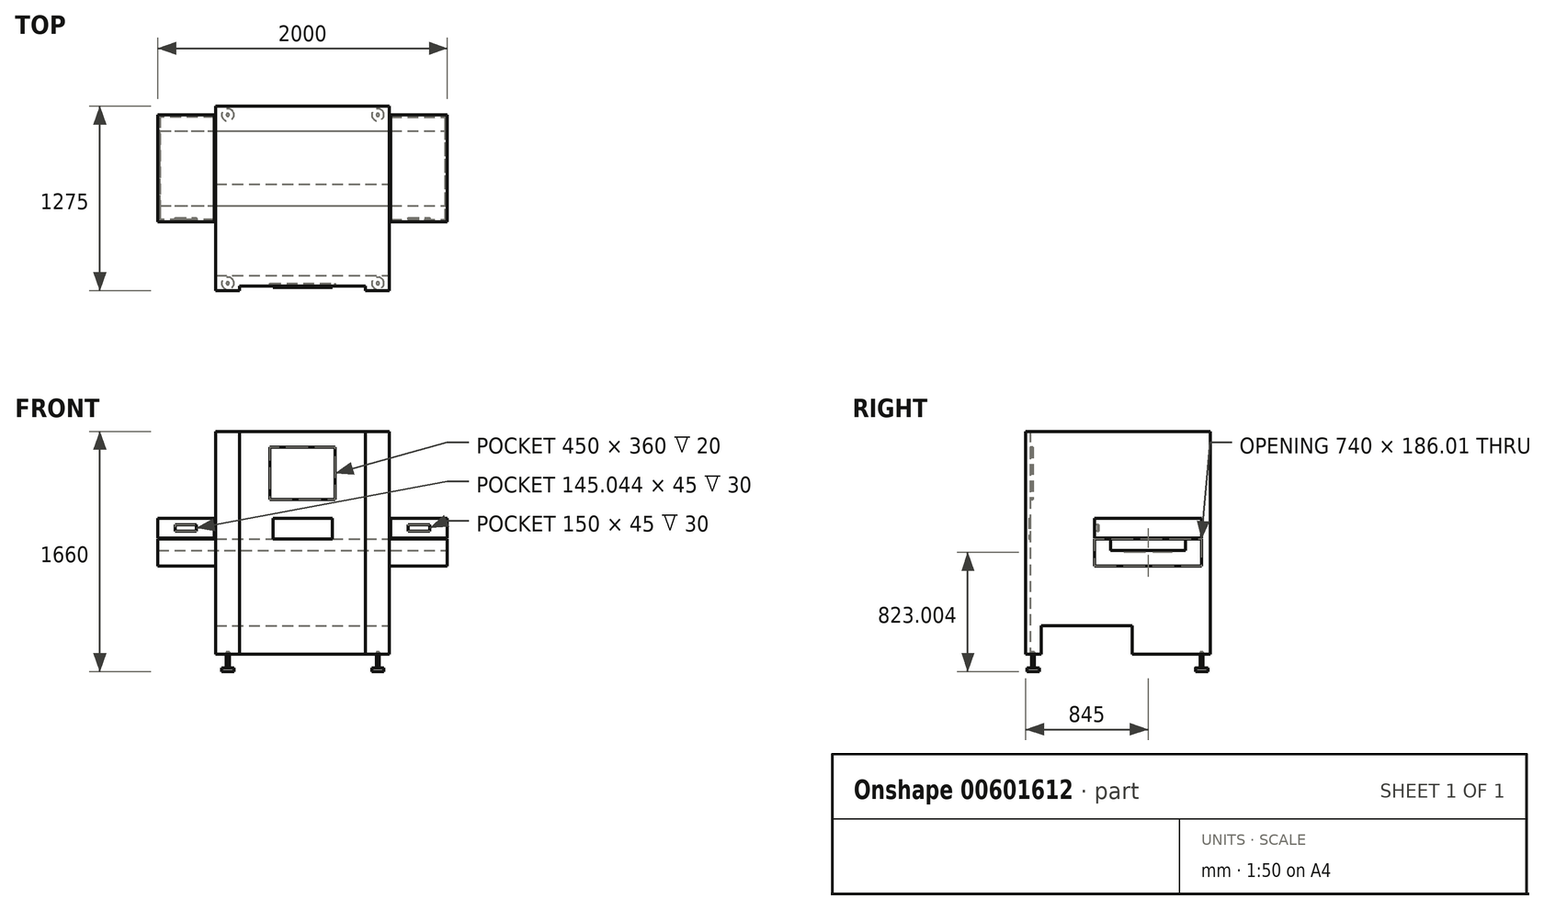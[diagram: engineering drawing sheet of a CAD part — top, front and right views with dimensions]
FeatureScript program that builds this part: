
annotation { "Feature Type Name" : "Feature", "Feature Type Description" : "" }
export const myFeature = defineFeature(function(context is Context, id is Id, definition is map)
    precondition{}
    {
        {
            var Q0;
            Q0=qCreatedBy(makeId("Top.planeOp"),FACE);
            var sketch = newSketch(context, id + "F0", { "sketchPlane" : qUnion([Q0])});
            skLineSegment(sketch, "E0.bottom", {"start": v(600, -637.5) * mm, "end": v(-600, -637.5) * mm});
            skLineSegment(sketch, "E0.top", {"start": v(600, 637.5) * mm, "end": v(-600, 637.5) * mm});
            skLineSegment(sketch, "E0.left", {"start": v(600, -637.5) * mm, "end": v(600, 637.5) * mm});
            skLineSegment(sketch, "E0.right", {"start": v(-600, -637.5) * mm, "end": v(-600, 637.5) * mm});
            skPoint(sketch, "E0.middle", {"position": v(0, 0) * mm});
            skSolve(sketch);
        }
        {
            var Q0;
            Q0=makeQuery(id+"F0.imprint","IMPRINT",FACE,{"disambiguationData":[TD([[makeQuery(id+"F0.imprint","IMPRINT",EDGE,{"derivedFrom":sQuery(id+"F0.wireOp",EDGE,"E0.bottom")}),-1.0]])]});
            extrude(context, id + "F1", {"entities" : qUnion([Q0]), "depth" : 1540 * mm, "offsetDistance" : 25 * mm});
        }
        {
            var Q0;
            Q0=makeQuery(id+"F1.opExtrude","CAP_FACE",FACE,{"disambiguationData":[OSD([sQuery(id+"F0.wireOp",EDGE,"E0.bottom"),sQuery(id+"F0.wireOp",EDGE,"E0.top"),sQuery(id+"F0.wireOp",EDGE,"E0.left"),sQuery(id+"F0.wireOp",EDGE,"E0.right")])],"isStart":true});
            var sketch = newSketch(context, id + "F2", { "sketchPlane" : qUnion([Q0])});
            skLineSegment(sketch, "E1.bottom", {"start": v(-600, 532.5) * mm, "end": v(600, 532.5) * mm});
            skLineSegment(sketch, "E1.top", {"start": v(-600, -97.5) * mm, "end": v(600, -97.5) * mm});
            skLineSegment(sketch, "E1.left", {"start": v(-600, 532.5) * mm, "end": v(-600, -97.5) * mm});
            skLineSegment(sketch, "E1.right", {"start": v(600, 532.5) * mm, "end": v(600, -97.5) * mm});
            skSolve(sketch);
        }
        {
            var Q0;
            Q0=makeQuery(id+"F2.imprint","IMPRINT",FACE,{"disambiguationData":[TD([[makeQuery(id+"F2.imprint","IMPRINT",EDGE,{"derivedFrom":sQuery(id+"F2.wireOp",EDGE,"E1.bottom")}),-1.0]])]});
            extrude(context, id + "F3", {"entities" : qUnion([Q0]), "operationType" : NewBodyOperationType.REMOVE, "oppositeDirection" : true, "depth" : 195 * mm, "offsetDistance" : 25 * mm});
        }
        {
            var Q0;
            Q0=makeQuery(id+"F1.opExtrude","SWEPT_FACE",FACE,{"disambiguationData":[OSD([sQuery(id+"F0.wireOp",EDGE,"E0.bottom")])]});
            var sketch = newSketch(context, id + "F4", { "sketchPlane" : qUnion([Q0])});
            skLineSegment(sketch, "E2.bottom", {"start": v(-435, 1540) * mm, "end": v(435, 1540) * mm});
            skLineSegment(sketch, "E2.top", {"start": v(-435, 0) * mm, "end": v(435, 0) * mm});
            skLineSegment(sketch, "E2.left", {"start": v(-435, 1540) * mm, "end": v(-435, 0) * mm});
            skLineSegment(sketch, "E2.right", {"start": v(435, 1540) * mm, "end": v(435, 0) * mm});
            skSolve(sketch);
        }
        {
            var Q0;
            Q0=makeQuery(id+"F4.imprint","IMPRINT",FACE,{"disambiguationData":[TD([[makeQuery(id+"F4.imprint","IMPRINT",EDGE,{"derivedFrom":sQuery(id+"F4.wireOp",EDGE,"E2.bottom")}),1.0]])]});
            extrude(context, id + "F5", {"entities" : qUnion([Q0]), "operationType" : NewBodyOperationType.REMOVE, "oppositeDirection" : true, "depth" : 30 * mm, "offsetDistance" : 25 * mm});
        }
        {
            var Q0;
            Q0=makeQuery(id+"F1.opExtrude","SWEPT_FACE",FACE,{"disambiguationData":[OSD([sQuery(id+"F0.wireOp",EDGE,"E0.left")])]});
            var sketch = newSketch(context, id + "F6", { "sketchPlane" : qUnion([Q0])});
            skLineSegment(sketch, "E3.bottom", {"start": v(-162.5, 940) * mm, "end": v(577.5, 940) * mm});
            skLineSegment(sketch, "E3.top", {"start": v(-162.5, 610) * mm, "end": v(577.5, 610) * mm});
            skLineSegment(sketch, "E3.left", {"start": v(-162.5, 940) * mm, "end": v(-162.5, 610) * mm});
            skLineSegment(sketch, "E3.right", {"start": v(577.5, 940) * mm, "end": v(577.5, 610) * mm});
            skSolve(sketch);
        }
        {
            var Q0;
            Q0=makeQuery(id+"F6.imprint","IMPRINT",FACE,{"disambiguationData":[TD([[makeQuery(id+"F6.imprint","IMPRINT",EDGE,{"derivedFrom":sQuery(id+"F6.wireOp",EDGE,"E3.bottom")}),-1.0]])]});
            extrude(context, id + "F7", {"entities" : qUnion([Q0]), "operationType" : NewBodyOperationType.ADD, "depth" : 400 * mm, "offsetDistance" : 25 * mm});
        }
        {
            var Q0;
            Q0=makeQuery(id+"F7.opExtrude","CAP_FACE",FACE,{"disambiguationData":[OSD([sQuery(id+"F6.wireOp",EDGE,"E3.bottom"),sQuery(id+"F6.wireOp",EDGE,"E3.top"),sQuery(id+"F6.wireOp",EDGE,"E3.left"),sQuery(id+"F6.wireOp",EDGE,"E3.right")])],"isStart":false});
            extrude(context, id + "F8", {"entities" : qUnion([Q0]), "operationType" : NewBodyOperationType.ADD, "oppositeDirection" : true, "depth" : 2000 * mm, "offsetDistance" : 25 * mm});
        }
        {
            var Q0;
            Q0=makeQuery(id+"F7.opExtrude","CAP_FACE",FACE,{"disambiguationData":[OSD([sQuery(id+"F6.wireOp",EDGE,"E3.bottom"),sQuery(id+"F6.wireOp",EDGE,"E3.top"),sQuery(id+"F6.wireOp",EDGE,"E3.left"),sQuery(id+"F6.wireOp",EDGE,"E3.right")])],"isStart":false});
            var sketch = newSketch(context, id + "F9", { "sketchPlane" : qUnion([Q0])});
            skLineSegment(sketch, "E4.bottom", {"start": v(-52.5, 796) * mm, "end": v(467.5, 796) * mm});
            skLineSegment(sketch, "E4.top", {"start": v(-52.5, 716) * mm, "end": v(467.5, 716) * mm});
            skLineSegment(sketch, "E4.left", {"start": v(-52.5, 796) * mm, "end": v(-52.5, 716) * mm});
            skLineSegment(sketch, "E4.right", {"start": v(467.5, 796) * mm, "end": v(467.5, 716) * mm});
            skSolve(sketch);
        }
        {
            var Q0;
            Q0=makeQuery(id+"F9.imprint","IMPRINT",FACE,{"disambiguationData":[TD([[makeQuery(id+"F9.imprint","IMPRINT",EDGE,{"derivedFrom":sQuery(id+"F9.wireOp",EDGE,"E4.bottom")}),-1.0]])]});
            extrude(context, id + "F10", {"entities" : qUnion([Q0]), "operationType" : NewBodyOperationType.REMOVE, "endBound" : BoundingType.THROUGH_ALL, "oppositeDirection" : true, "depth" : 25 * mm, "offsetDistance" : 25 * mm});
        }
        {
            var Q0;
            Q0=makeQuery(id+"F5.boolean.opBoolean","COPY",FACE,{"derivedFrom":makeQuery(id+"F5.opExtrude","CAP_FACE",FACE,{"disambiguationData":[OSD([sQuery(id+"F4.wireOp",EDGE,"E2.bottom"),sQuery(id+"F4.wireOp",EDGE,"E2.top"),sQuery(id+"F4.wireOp",EDGE,"E2.left"),sQuery(id+"F4.wireOp",EDGE,"E2.right")])],"isStart":false})});
            var sketch = newSketch(context, id + "F11", { "sketchPlane" : qUnion([Q0])});
            skLineSegment(sketch, "E5.bottom", {"start": v(-225, 1430) * mm, "end": v(225, 1430) * mm});
            skLineSegment(sketch, "E5.top", {"start": v(-225, 1070) * mm, "end": v(225, 1070) * mm});
            skLineSegment(sketch, "E5.left", {"start": v(-225, 1430) * mm, "end": v(-225, 1070) * mm});
            skLineSegment(sketch, "E5.right", {"start": v(225, 1430) * mm, "end": v(225, 1070) * mm});
            skSolve(sketch);
        }
        {
            var Q0;
            Q0=makeQuery(id+"F11.imprint","IMPRINT",FACE,{"disambiguationData":[TD([[makeQuery(id+"F11.imprint","IMPRINT",EDGE,{"derivedFrom":sQuery(id+"F11.wireOp",EDGE,"E5.bottom")}),-1.0]])]});
            extrude(context, id + "F12", {"entities" : qUnion([Q0]), "operationType" : NewBodyOperationType.REMOVE, "oppositeDirection" : true, "depth" : 20 * mm, "offsetDistance" : 25 * mm});
        }
        {
            var Q0;
            Q0=makeQuery(id+"F12.boolean.opBoolean","COPY",FACE,{"derivedFrom":makeQuery(id+"F12.opExtrude","CAP_FACE",FACE,{"disambiguationData":[OSD([sQuery(id+"F11.wireOp",EDGE,"E5.bottom"),sQuery(id+"F11.wireOp",EDGE,"E5.top"),sQuery(id+"F11.wireOp",EDGE,"E5.left"),sQuery(id+"F11.wireOp",EDGE,"E5.right")])],"isStart":false})});
            extrude(context, id + "F13", {"entities" : qUnion([Q0]), "depth" : 10 * mm, "offsetDistance" : 25 * mm});
        }
        {
            var Q0;
            Q0=makeQuery(id+"F7.opExtrude","SWEPT_FACE",FACE,{"disambiguationData":[OSD([sQuery(id+"F6.wireOp",EDGE,"E3.left")])]});
            var sketch = newSketch(context, id + "F14", { "sketchPlane" : qUnion([Q0])});
            skLineSegment(sketch, "E6.bottom", {"start": v(600, 940) * mm, "end": v(610, 940) * mm});
            skLineSegment(sketch, "E6.top", {"start": v(600, 795) * mm, "end": v(610, 795) * mm});
            skLineSegment(sketch, "E6.left", {"start": v(600, 940) * mm, "end": v(600, 795) * mm});
            skLineSegment(sketch, "E6.right", {"start": v(610, 940) * mm, "end": v(610, 795) * mm});
            skSolve(sketch);
        }
        {
            var Q0;
            Q0=makeQuery(id+"F14.imprint","IMPRINT",FACE,{"disambiguationData":[TD([[makeQuery(id+"F14.imprint","IMPRINT",EDGE,{"derivedFrom":sQuery(id+"F14.wireOp",EDGE,"E6.bottom")}),1.0]])]});
            extrude(context, id + "F15", {"entities" : qUnion([Q0]), "operationType" : NewBodyOperationType.REMOVE, "endBound" : BoundingType.THROUGH_ALL, "oppositeDirection" : true, "depth" : 25 * mm, "offsetDistance" : 25 * mm});
        }
        {
            var Q0;
            Q0=makeQuery(id+"F8.opExtrude","SWEPT_FACE",FACE,{"disambiguationData":[OSD([sQuery(id+"F6.wireOp",EDGE,"E3.left")])]});
            var sketch = newSketch(context, id + "F16", { "sketchPlane" : qUnion([Q0])});
            skLineSegment(sketch, "E7.bottom", {"start": v(-600, 940) * mm, "end": v(-610, 940) * mm});
            skLineSegment(sketch, "E7.top", {"start": v(-600, 795) * mm, "end": v(-610, 795) * mm});
            skLineSegment(sketch, "E7.left", {"start": v(-600, 940) * mm, "end": v(-600, 795) * mm});
            skLineSegment(sketch, "E7.right", {"start": v(-610, 940) * mm, "end": v(-610, 795) * mm});
            skSolve(sketch);
        }
        {
            var Q0;
            Q0=makeQuery(id+"F16.imprint","IMPRINT",FACE,{"disambiguationData":[TD([[makeQuery(id+"F16.imprint","IMPRINT",EDGE,{"derivedFrom":sQuery(id+"F16.wireOp",EDGE,"E7.bottom")}),-1.0]])]});
            extrude(context, id + "F17", {"entities" : qUnion([Q0]), "operationType" : NewBodyOperationType.REMOVE, "endBound" : BoundingType.THROUGH_ALL, "oppositeDirection" : true, "depth" : 25 * mm, "offsetDistance" : 25 * mm});
        }
        {
            var Q0;
            Q0=makeQuery(id+"F8.opExtrude","SWEPT_FACE",FACE,{"disambiguationData":[OSD([sQuery(id+"F6.wireOp",EDGE,"E3.left")])]});
            var sketch = newSketch(context, id + "F18", { "sketchPlane" : qUnion([Q0])});
            skLineSegment(sketch, "E8.bottom", {"start": v(-610, 795) * mm, "end": v(-1000, 795) * mm});
            skLineSegment(sketch, "E8.top", {"start": v(-610, 802) * mm, "end": v(-1000, 802) * mm});
            skLineSegment(sketch, "E8.left", {"start": v(-610, 795) * mm, "end": v(-610, 802) * mm});
            skLineSegment(sketch, "E8.right", {"start": v(-1000, 795) * mm, "end": v(-1000, 802) * mm});
            skSolve(sketch);
        }
        {
            var Q0;
            Q0=makeQuery(id+"F18.imprint","IMPRINT",FACE,{"disambiguationData":[TD([[makeQuery(id+"F18.imprint","IMPRINT",EDGE,{"derivedFrom":sQuery(id+"F18.wireOp",EDGE,"E8.bottom")}),-1.0]])]});
            extrude(context, id + "F19", {"entities" : qUnion([Q0]), "operationType" : NewBodyOperationType.REMOVE, "oppositeDirection" : true, "depth" : 15 * mm, "offsetDistance" : 25 * mm});
        }
        {
            var Q0;
            Q0=makeQuery(id+"F7.opExtrude","SWEPT_FACE",FACE,{"disambiguationData":[OSD([sQuery(id+"F6.wireOp",EDGE,"E3.left")])]});
            var sketch = newSketch(context, id + "F20", { "sketchPlane" : qUnion([Q0])});
            skLineSegment(sketch, "E9.bottom", {"start": v(610, 795) * mm, "end": v(1000, 795) * mm});
            skLineSegment(sketch, "E9.top", {"start": v(610, 802) * mm, "end": v(1000, 802) * mm});
            skLineSegment(sketch, "E9.left", {"start": v(610, 795) * mm, "end": v(610, 802) * mm});
            skLineSegment(sketch, "E9.right", {"start": v(1000, 795) * mm, "end": v(1000, 802) * mm});
            skSolve(sketch);
        }
        {
            var Q0;
            Q0=makeQuery(id+"F20.imprint","IMPRINT",FACE,{"disambiguationData":[TD([[makeQuery(id+"F20.imprint","IMPRINT",EDGE,{"derivedFrom":sQuery(id+"F20.wireOp",EDGE,"E9.bottom")}),1.0]])]});
            extrude(context, id + "F21", {"entities" : qUnion([Q0]), "operationType" : NewBodyOperationType.REMOVE, "oppositeDirection" : true, "depth" : 15 * mm, "offsetDistance" : 25 * mm});
        }
        {
            var Q0;
            Q0=makeQuery(id+"F7.opExtrude","CAP_FACE",FACE,{"disambiguationData":[OSD([sQuery(id+"F6.wireOp",EDGE,"E3.bottom"),sQuery(id+"F6.wireOp",EDGE,"E3.top"),sQuery(id+"F6.wireOp",EDGE,"E3.left"),sQuery(id+"F6.wireOp",EDGE,"E3.right")])],"isStart":false});
            var sketch = newSketch(context, id + "F22", { "sketchPlane" : qUnion([Q0])});
            skLineSegment(sketch, "E10.bottom", {"start": v(-147.5, 802) * mm, "end": v(577.5, 802) * mm});
            skLineSegment(sketch, "E10.top", {"start": v(-147.5, 795) * mm, "end": v(577.5, 795) * mm});
            skLineSegment(sketch, "E10.left", {"start": v(-147.5, 802) * mm, "end": v(-147.5, 795) * mm});
            skLineSegment(sketch, "E10.right", {"start": v(577.5, 802) * mm, "end": v(577.5, 795) * mm});
            skSolve(sketch);
        }
        {
            var Q0;
            Q0=makeQuery(id+"F22.imprint","IMPRINT",FACE,{"disambiguationData":[TD([[makeQuery(id+"F22.imprint","IMPRINT",EDGE,{"derivedFrom":sQuery(id+"F22.wireOp",EDGE,"E10.bottom")}),-1.0]])]});
            extrude(context, id + "F23", {"entities" : qUnion([Q0]), "operationType" : NewBodyOperationType.REMOVE, "oppositeDirection" : true, "depth" : 15 * mm, "offsetDistance" : 25 * mm});
        }
        {
            var Q0;
            Q0=makeQuery(id+"F7.opExtrude","SWEPT_FACE",FACE,{"disambiguationData":[OSD([sQuery(id+"F6.wireOp",EDGE,"E3.right")])]});
            var sketch = newSketch(context, id + "F24", { "sketchPlane" : qUnion([Q0])});
            skLineSegment(sketch, "E11.bottom", {"start": v(-610, 795) * mm, "end": v(-985, 795) * mm});
            skLineSegment(sketch, "E11.top", {"start": v(-610, 802) * mm, "end": v(-985, 802) * mm});
            skLineSegment(sketch, "E11.left", {"start": v(-610, 795) * mm, "end": v(-610, 802) * mm});
            skLineSegment(sketch, "E11.right", {"start": v(-985, 795) * mm, "end": v(-985, 802) * mm});
            skSolve(sketch);
        }
        {
            var Q0;
            Q0=makeQuery(id+"F24.imprint","IMPRINT",FACE,{"disambiguationData":[TD([[makeQuery(id+"F24.imprint","IMPRINT",EDGE,{"derivedFrom":sQuery(id+"F24.wireOp",EDGE,"E11.bottom")}),-1.0]])]});
            extrude(context, id + "F25", {"entities" : qUnion([Q0]), "operationType" : NewBodyOperationType.REMOVE, "oppositeDirection" : true, "depth" : 15 * mm, "offsetDistance" : 25 * mm});
        }
        {
            var Q0;
            Q0=makeQuery(id+"F8.opExtrude","SWEPT_FACE",FACE,{"disambiguationData":[OSD([sQuery(id+"F6.wireOp",EDGE,"E3.right")])]});
            var sketch = newSketch(context, id + "F26", { "sketchPlane" : qUnion([Q0])});
            skLineSegment(sketch, "E12.bottom", {"start": v(610, 795) * mm, "end": v(1000, 795) * mm});
            skLineSegment(sketch, "E12.top", {"start": v(610, 802) * mm, "end": v(1000, 802) * mm});
            skLineSegment(sketch, "E12.left", {"start": v(610, 795) * mm, "end": v(610, 802) * mm});
            skLineSegment(sketch, "E12.right", {"start": v(1000, 795) * mm, "end": v(1000, 802) * mm});
            skSolve(sketch);
        }
        {
            var Q0;
            Q0=makeQuery(id+"F26.imprint","IMPRINT",FACE,{"disambiguationData":[TD([[makeQuery(id+"F26.imprint","IMPRINT",EDGE,{"derivedFrom":sQuery(id+"F26.wireOp",EDGE,"E12.bottom")}),1.0]])]});
            extrude(context, id + "F27", {"entities" : qUnion([Q0]), "operationType" : NewBodyOperationType.REMOVE, "oppositeDirection" : true, "depth" : 15 * mm, "offsetDistance" : 25 * mm});
        }
        {
            var Q0;
            Q0=makeQuery(id+"F8.opExtrude","CAP_FACE",FACE,{"disambiguationData":[OSD([sQuery(id+"F6.wireOp",EDGE,"E3.bottom"),sQuery(id+"F6.wireOp",EDGE,"E3.top"),sQuery(id+"F6.wireOp",EDGE,"E3.left"),sQuery(id+"F6.wireOp",EDGE,"E3.right")])],"isStart":false});
            var sketch = newSketch(context, id + "F28", { "sketchPlane" : qUnion([Q0])});
            skLineSegment(sketch, "E13.bottom", {"start": v(-562.5, 802) * mm, "end": v(147.5, 802) * mm});
            skLineSegment(sketch, "E13.top", {"start": v(-562.5, 795) * mm, "end": v(147.5, 795) * mm});
            skLineSegment(sketch, "E13.left", {"start": v(-562.5, 802) * mm, "end": v(-562.5, 795) * mm});
            skLineSegment(sketch, "E13.right", {"start": v(147.5, 802) * mm, "end": v(147.5, 795) * mm});
            skSolve(sketch);
        }
        {
            var Q0;
            Q0=makeQuery(id+"F28.imprint","IMPRINT",FACE,{"disambiguationData":[TD([[makeQuery(id+"F28.imprint","IMPRINT",EDGE,{"derivedFrom":sQuery(id+"F28.wireOp",EDGE,"E13.bottom")}),-1.0]])]});
            extrude(context, id + "F29", {"entities" : qUnion([Q0]), "operationType" : NewBodyOperationType.REMOVE, "oppositeDirection" : true, "depth" : 15 * mm, "offsetDistance" : 25 * mm});
        }
        {
            var Q0;
            Q0=makeQuery(id+"F5.boolean.opBoolean","COPY",FACE,{"derivedFrom":makeQuery(id+"F5.opExtrude","CAP_FACE",FACE,{"disambiguationData":[OSD([sQuery(id+"F4.wireOp",EDGE,"E2.bottom"),sQuery(id+"F4.wireOp",EDGE,"E2.top"),sQuery(id+"F4.wireOp",EDGE,"E2.left"),sQuery(id+"F4.wireOp",EDGE,"E2.right")])],"isStart":false})});
            var sketch = newSketch(context, id + "F30", { "sketchPlane" : qUnion([Q0])});
            skLineSegment(sketch, "E14.bottom", {"start": v(-205, 940) * mm, "end": v(205, 940) * mm});
            skLineSegment(sketch, "E14.top", {"start": v(-205, 795) * mm, "end": v(205, 795) * mm});
            skLineSegment(sketch, "E14.left", {"start": v(-205, 940) * mm, "end": v(-205, 795) * mm});
            skLineSegment(sketch, "E14.right", {"start": v(205, 940) * mm, "end": v(205, 795) * mm});
            skSolve(sketch);
        }
        {
            var Q0;
            Q0=makeQuery(id+"F30.imprint","IMPRINT",FACE,{"disambiguationData":[TD([[makeQuery(id+"F30.imprint","IMPRINT",EDGE,{"derivedFrom":sQuery(id+"F30.wireOp",EDGE,"E14.bottom")}),-1.0]])]});
            extrude(context, id + "F31", {"entities" : qUnion([Q0]), "operationType" : NewBodyOperationType.ADD, "depth" : 10 * mm, "offsetDistance" : 25 * mm});
        }
        {
            var Q0;
            {var subQ0=sQuery(id+"F6.wireOp",EDGE,"E3.bottom");var subQ1=sQuery(id+"F6.wireOp",EDGE,"E3.left");Q0=makeQuery(id+"F19.boolean.opBoolean","SPLIT",FACE,{"disambiguationData":[TD([makeQuery(id+"F8.opExtrude","SWEPT_FACE",FACE,{"disambiguationData":[OSD([subQ0])]})])],"derivedFrom":makeQuery(id+"F8.opExtrude","SWEPT_FACE",FACE,{"disambiguationData":[OSD([subQ1])]})});}
            var sketch = newSketch(context, id + "F32", { "sketchPlane" : qUnion([Q0])});
            skLineSegment(sketch, "E15.bottom", {"start": v(-880, 894) * mm, "end": v(-730, 894) * mm});
            skLineSegment(sketch, "E15.top", {"start": v(-880, 849) * mm, "end": v(-734.96, 849) * mm});
            skLineSegment(sketch, "E15.left", {"start": v(-880, 894) * mm, "end": v(-880, 849) * mm});
            skLineSegment(sketch, "E15.right", {"start": v(-734.96, 894) * mm, "end": v(-734.96, 849) * mm});
            skSolve(sketch);
        }
        {
            var Q0;
            Q0=makeQuery(id+"F32.imprint","IMPRINT",FACE,{"disambiguationData":[TD([[makeQuery(id+"F32.imprint","IMPRINT",EDGE,{"derivedFrom":sQuery(id+"F32.wireOp",EDGE,"E15.top")}),1.0]])]});
            extrude(context, id + "F33", {"entities" : qUnion([Q0]), "operationType" : NewBodyOperationType.REMOVE, "oppositeDirection" : true, "depth" : 30 * mm, "offsetDistance" : 25 * mm});
        }
        {
            var Q0;
            Q0=makeQuery(id+"F33.boolean.opBoolean","COPY",FACE,{"derivedFrom":makeQuery(id+"F33.opExtrude","CAP_FACE",FACE,{"disambiguationData":[OSD([sQuery(id+"F32.wireOp",EDGE,"E15.bottom"),sQuery(id+"F32.wireOp",EDGE,"E15.top"),sQuery(id+"F32.wireOp",EDGE,"E15.left"),sQuery(id+"F32.wireOp",EDGE,"E15.right")])],"isStart":false})});
            extrude(context, id + "F34", {"entities" : qUnion([Q0]), "depth" : 10 * mm, "offsetDistance" : 25 * mm});
        }
        {
            var Q0;
            {var subQ0=sQuery(id+"F6.wireOp",EDGE,"E3.bottom");var subQ1=sQuery(id+"F6.wireOp",EDGE,"E3.left");Q0=makeQuery(id+"F21.boolean.opBoolean","SPLIT",FACE,{"disambiguationData":[TD([makeQuery(id+"F7.opExtrude","SWEPT_FACE",FACE,{"disambiguationData":[OSD([subQ0])]})])],"derivedFrom":makeQuery(id+"F7.opExtrude","SWEPT_FACE",FACE,{"disambiguationData":[OSD([subQ1])]})});}
            var sketch = newSketch(context, id + "F35", { "sketchPlane" : qUnion([Q0])});
            skLineSegment(sketch, "E16.bottom", {"start": v(730, 894) * mm, "end": v(880, 894) * mm});
            skLineSegment(sketch, "E16.top", {"start": v(730, 849) * mm, "end": v(880, 849) * mm});
            skLineSegment(sketch, "E16.left", {"start": v(730, 894) * mm, "end": v(730, 849) * mm});
            skLineSegment(sketch, "E16.right", {"start": v(880, 894) * mm, "end": v(880, 849) * mm});
            skSolve(sketch);
        }
        {
            var Q0;
            Q0=makeQuery(id+"F35.imprint","IMPRINT",FACE,{"disambiguationData":[TD([[makeQuery(id+"F35.imprint","IMPRINT",EDGE,{"derivedFrom":sQuery(id+"F35.wireOp",EDGE,"E16.bottom")}),-1.0]])]});
            extrude(context, id + "F36", {"entities" : qUnion([Q0]), "operationType" : NewBodyOperationType.REMOVE, "oppositeDirection" : true, "depth" : 30 * mm, "offsetDistance" : 25 * mm});
        }
        {
            var Q0;
            Q0=makeQuery(id+"F36.boolean.opBoolean","COPY",FACE,{"derivedFrom":makeQuery(id+"F36.opExtrude","CAP_FACE",FACE,{"disambiguationData":[OSD([sQuery(id+"F35.wireOp",EDGE,"E16.bottom"),sQuery(id+"F35.wireOp",EDGE,"E16.top"),sQuery(id+"F35.wireOp",EDGE,"E16.left"),sQuery(id+"F35.wireOp",EDGE,"E16.right")])],"isStart":false})});
            extrude(context, id + "F37", {"entities" : qUnion([Q0]), "depth" : 10 * mm, "offsetDistance" : 25 * mm});
        }
        {
            var Q0;
            Q0=makeQuery(id+"F37.opExtrude","SWEPT_BODY",BODY,{"disambiguationData":[OSD([sQuery(id+"F35.wireOp",EDGE,"E16.bottom"),sQuery(id+"F35.wireOp",EDGE,"E16.top"),sQuery(id+"F35.wireOp",EDGE,"E16.left"),sQuery(id+"F35.wireOp",EDGE,"E16.right")])]});
            var Q1;
            Q1=makeQuery(id+"F34.opExtrude","SWEPT_BODY",BODY,{"disambiguationData":[OSD([sQuery(id+"F32.wireOp",EDGE,"E15.bottom"),sQuery(id+"F32.wireOp",EDGE,"E15.top"),sQuery(id+"F32.wireOp",EDGE,"E15.left"),sQuery(id+"F32.wireOp",EDGE,"E15.right")])]});
            var Q2;
            Q2=makeQuery(id+"F13.opExtrude","SWEPT_BODY",BODY,{"disambiguationData":[OSD([sQuery(id+"F11.wireOp",EDGE,"E5.bottom"),sQuery(id+"F11.wireOp",EDGE,"E5.top"),sQuery(id+"F11.wireOp",EDGE,"E5.left"),sQuery(id+"F11.wireOp",EDGE,"E5.right")])]});
            var Q3;
            Q3=makeQuery(id+"F1.opExtrude","SWEPT_BODY",BODY,{"disambiguationData":[OSD([sQuery(id+"F0.wireOp",EDGE,"E0.bottom"),sQuery(id+"F0.wireOp",EDGE,"E0.top"),sQuery(id+"F0.wireOp",EDGE,"E0.left"),sQuery(id+"F0.wireOp",EDGE,"E0.right")])]});
            transform(context, id + "F38", {"entities" : qUnion([Q0, Q1, Q2, Q3]), "transformType" : TransformType.TRANSLATION_3D, "dx" : 0 * mm, "dy" : 0 * mm, "dz" : 120 * mm, "makeCopy" : false});
        }
        {
            var Q0;
            Q0=qCreatedBy(makeId("Top.planeOp"),FACE);
            var sketch = newSketch(context, id + "F39", { "sketchPlane" : qUnion([Q0])});
            skCircle(sketch, "E17", {"center": v(0, 0) * mm, "radius": 42.5 * mm});
            skSolve(sketch);
        }
        {
            var Q0;
            Q0=makeQuery(id+"F39.imprint","IMPRINT",FACE,{"disambiguationData":[TD([[makeQuery(id+"F39.imprint","IMPRINT",EDGE,{"derivedFrom":sQuery(id+"F39.wireOp",EDGE,"E17")}),1.0]])]});
            extrude(context, id + "F40", {"entities" : qUnion([Q0]), "depth" : 25 * mm, "offsetDistance" : 25 * mm});
        }
        {
            var Q0;
            Q0=makeQuery(id+"F40.opExtrude","CAP_FACE",FACE,{"disambiguationData":[OSD([sQuery(id+"F39.wireOp",EDGE,"E17")])],"isStart":false});
            var sketch = newSketch(context, id + "F41", { "sketchPlane" : qUnion([Q0])});
            skCircle(sketch, "E18", {"center": v(0, 0) * mm, "radius": 10 * mm});
            skSolve(sketch);
        }
        {
            var Q0;
            Q0=makeQuery(id+"F41.imprint","IMPRINT",FACE,{"disambiguationData":[TD([[makeQuery(id+"F41.imprint","IMPRINT",EDGE,{"derivedFrom":sQuery(id+"F41.wireOp",EDGE,"E18")}),1.0]])]});
            extrude(context, id + "F42", {"entities" : qUnion([Q0]), "operationType" : NewBodyOperationType.ADD, "depth" : 110 * mm, "offsetDistance" : 25 * mm});
        }
        {
            var Q0;
            Q0=makeQuery(id+"F40.opExtrude","SWEPT_BODY",BODY,{"disambiguationData":[OSD([sQuery(id+"F39.wireOp",EDGE,"E17")])]});
            transform(context, id + "F43", {"entities" : qUnion([Q0]), "transformType" : TransformType.TRANSLATION_3D, "dx" : -517 * mm, "dy" : 0 * mm, "dz" : 0 * mm, "makeCopy" : false});
        }
        {
            var Q0;
            Q0=makeQuery(id+"F40.opExtrude","SWEPT_BODY",BODY,{"disambiguationData":[OSD([sQuery(id+"F39.wireOp",EDGE,"E17")])]});
            transform(context, id + "F44", {"entities" : qUnion([Q0]), "transformType" : TransformType.TRANSLATION_3D, "dx" : 1037 * mm, "dy" : 0 * mm, "dz" : 0 * mm, "makeCopy" : true});
        }
        {
            var Q0;
            Q0=makeQuery(id+"F44.opPattern","COPY",BODY,{"derivedFrom":makeQuery(id+"F40.opExtrude","SWEPT_BODY",BODY,{"disambiguationData":[OSD([sQuery(id+"F39.wireOp",EDGE,"E17")])]}),"instanceName":"1"});
            var Q1;
            Q1=makeQuery(id+"F40.opExtrude","SWEPT_BODY",BODY,{"disambiguationData":[OSD([sQuery(id+"F39.wireOp",EDGE,"E17")])]});
            transform(context, id + "F45", {"entities" : qUnion([Q0, Q1]), "transformType" : TransformType.TRANSLATION_3D, "dx" : 0 * mm, "dy" : -587 * mm, "dz" : 0 * mm, "makeCopy" : false});
        }
        {
            var Q0;
            Q0=makeQuery(id+"F44.opPattern","COPY",BODY,{"derivedFrom":makeQuery(id+"F40.opExtrude","SWEPT_BODY",BODY,{"disambiguationData":[OSD([sQuery(id+"F39.wireOp",EDGE,"E17")])]}),"instanceName":"1"});
            var Q1;
            Q1=makeQuery(id+"F40.opExtrude","SWEPT_BODY",BODY,{"disambiguationData":[OSD([sQuery(id+"F39.wireOp",EDGE,"E17")])]});
            transform(context, id + "F46", {"entities" : qUnion([Q0, Q1]), "transformType" : TransformType.TRANSLATION_3D, "dx" : 0 * mm, "dy" : 1165 * mm, "dz" : 0 * mm, "makeCopy" : true});
        }
    });
